# Revit family: 80HS0206_BIMOpen
name_source: partatom
category: Specialty Equipment
units: mm (PartAtom-declared; Revit-internal decimal feet)

## family parameters
Always vertical = Yes
Cut with Voids When Loaded = No
Host = Wall
Part Type = Normal
Room Calculation Point = No
Round Connector Dimension = Use Diameter
Shared = No

## types (1)
- 80HS0206 OPEN
    Adjustable Height = 36"
    Configuration = Open
    Description = Ascent 76 Universal Changing Station
    Elevation = 0"
    Frame Finish = Stainless Steel Finish
    Manufacturer = The Sova Company
    Material(s) = Powder Coated Cold Rolled Steel, Stainless Steel and ABS
    Model = 800SS-01 Open
    Panel Finish = Stainless Steel Finish
    Product Site = https://choosesova.com
    Product Weight = 400lb
    SKU = 800SS-01
    Shipping Height = 18"
    Shipping Length = 81"
    Shipping Width = 48"
    URL = https://choosesova.com
    Unit Height = 69"
    Unit Length = 76 1/2"
    Unit Width = 41"
    Weight Capacity = 500lb

## geometry (parser evidence)
native form markers: Sweep x8
no freeform markers — native parametric forms only
